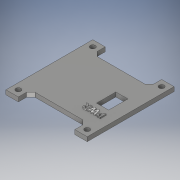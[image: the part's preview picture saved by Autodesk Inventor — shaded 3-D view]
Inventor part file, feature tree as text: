
AUTODESK INVENTOR PART (.ipt)
format: ipt  version: 2018 (Build 220112000, 112)  size: 1,312,256 bytes
history: native  units: in
note: dims shown in document units (in); Inventor stores cm internally (conversion verified against a paired STEP export)
features: sketch x4, extrude x3, move_body x3, direct_edit x2, emboss x1, chamfer x1
ambient origin geometry x8: Origin, YZ Plane, XZ Plane, XY Plane, X Axis, Y Axis, Z Axis, Center Point
bodies: Solid1 (feature_tree)
feature tree (14):
  extrude  "Extrusion1"  Depth=0.36in
  extrude  "Extrusion2"  Depth=0.36in
  extrude  "Extrusion3"  Depth=0.36in
  emboss  "Emboss1"
  chamfer  "Chamfer1"  Distance=0.125in
  direct_edit  "Direct Edit1"
  direct_edit  "Direct Edit2"
  sketch  "Sketch1"  dims[d0=2.311in d1=0.36in]
  sketch  "Sketch2"  dims[d2=0.36in d3=0.36in]
  sketch  "Sketch3"  dims[d4=0.36in d5=0.36in]
  sketch  "Sketch5"  dims[d7=0.36in d8=0.125in d9=0.0in d10=0.146in d11=0.146in d12=0.146in d13=0.146in d14=1.0in d15=0.0in d16=3.9in d17=0.18in d18=0.181in d19=0.18in d20=0.18in d21=0.181in d22=0.18in d23=0.18in d24=0.18in d25=0.56in d26=0.35in d27=0.35in d28=0.25in d30=1.0in d31=0.0in d32=0.36in d37=0.035in d38=0.0in d64=0.125in d65=0.125in d66=45.0deg d67=0.0in d68=0.0in d69=0.105in d70=0.0in d71=0.0in d72=0.105in d73=0.0in d74=0.0in d75=-1.54in]
  move_body  "Move1"
  move_body  "Move2"
  move_body  "Move3"
